# Revit family: W20AS
name_source: partatom
category: Plumbing Fixtures
revit_build: Autodesk Revit 2016 (Build: 20190508_0715(x64)
units: mm (PartAtom-declared; Revit-internal decimal feet)

## family parameters
Always vertical = Yes
Cut with Voids When Loaded = No
Part Type = Normal
Room Calculation Point = No
Round Connector Dimension = Use Diameter
Shared = No
Work Plane-Based = No

## types (16) — shared parameters
Manufacturer = SanSwiss
Model = W20AS
Type Comments = LIVADA
URL = http://www.sanswiss.com

## per-type parameters (varying)
| type | A | B |
| 700x1200 | 700 mm  [stored 2.29659 ft] | 1200 mm |
| 800x1400 | 800 mm  [stored 2.62467 ft] | 1400 mm  [stored 4.59318 ft] |
| 700x1400 | 700 mm  [stored 2.29659 ft] | 1400 mm  [stored 4.59318 ft] |
| 900x1200 | 900 mm  [stored 2.95276 ft] | 1200 mm |
| 700x1600 | 700 mm  [stored 2.29659 ft] | 1600 mm  [stored 5.24934 ft] |
| 800x1200 | 800 mm  [stored 2.62467 ft] | 1200 mm |
| 800x1600 | 800 mm  [stored 2.62467 ft] | 1600 mm  [stored 5.24934 ft] |
| 900x1600 | 900 mm  [stored 2.95276 ft] | 1600 mm  [stored 5.24934 ft] |
| 900x1400 | 900 mm  [stored 2.95276 ft] | 1400 mm  [stored 4.59318 ft] |
| 700x900 | 700 mm  [stored 2.29659 ft] | 900 mm  [stored 2.95276 ft] |
| 700x1000 | 700 mm  [stored 2.29659 ft] | 1000 mm  [stored 3.28084 ft] |
| 800x900 | 800 mm  [stored 2.62467 ft] | 900 mm  [stored 2.95276 ft] |
| 800x1000 | 800 mm  [stored 2.62467 ft] | 1000 mm  [stored 3.28084 ft] |
| 800x1100 | 800 mm  [stored 2.62467 ft] | 1100 mm |
| 900x1000 | 900 mm  [stored 2.95276 ft] | 1000 mm  [stored 3.28084 ft] |
| 900x1100 | 900 mm  [stored 2.95276 ft] | 1100 mm |

note: [stored X ft] marks values corroborated as IEEE doubles in the binary element streams (Revit-internal decimal feet)

## geometry (parser evidence)
native form markers: Sweep x3
no freeform markers — native parametric forms only
